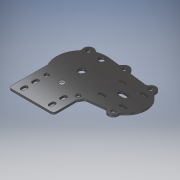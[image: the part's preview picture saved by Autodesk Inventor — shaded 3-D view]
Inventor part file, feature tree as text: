
AUTODESK INVENTOR PART (.ipt)
format: ipt  version: 2017 (Build 210142000, 142)  size: 376,320 bytes
history: native  units: mm
features: extrude x8, sketch x6, fillet x2, other x1, mirror x1
ambient origin geometry x8: Origin, YZ Plane, XZ Plane, XY Plane, X Axis, Y Axis, Z Axis, Center Point
bodies: Body1 (feature_tree)
feature tree (18):
  other  "Sólido1"
  extrude  "Extrusión1"  Depth=88.9mm
  sketch  "Boceto2"  dims[d2=203.2mm d3=22.225mm d4=22.225mm]
  extrude  "Extrusión2"  Depth=22.225mm
  fillet  "Empalme1"  Radius=22.225mm
  sketch  "Boceto3"  dims[d7=22.225mm d8=22.225mm]
  extrude  "Extrusión3"  Depth=22.225mm
  extrude  "Extrusión4"  TaperAngle=0.0deg  [1 undecoded]
  extrude  "Extrusión5"  Depth=4.445mm TaperAngle=0.0deg
  extrude  "Extrusión6"  Depth=6.35mm
  extrude  "Extrusión7"  Depth=6.35mm
  mirror  "Simetría1"
  fillet  "Empalme2"  Radius=9.525mm
  extrude  "Extrusión8"  Depth=6.35mm
  sketch  "Boceto1"  dims[d0=114.3mm d1=88.9mm]
  sketch  "Boceto4"  dims[d11=22.225mm d13=0.0mm]
  sketch  "Boceto5"  dims[d14=22.225mm d16=4.445mm d17=0.0mm]
  sketch  "Boceto7"  dims[d18=9.525mm d19=9.525mm d20=9.525mm d21=9.525mm d22=9.525mm d23=9.525mm d24=25.4mm d25=0.0mm d26=6.35mm d27=12.7mm d28=12.7mm d29=44.45mm d30=44.45mm d31=31.75mm d32=31.75mm d33=14.2875mm d34=12.7mm d35=12.7mm d36=45.0mm d37=45.0mm d38=25.4mm d39=0.0mm d40=11.1125mm d41=56.0mm d42=56.0mm d43=28.0mm d44=28.0mm d45=0.0mm d46=93.4212mm d47=47.5mm d48=47.5mm d49=23.75mm d50=23.75mm d57=5.55625mm d58=5.159375mm d59=5.55625mm d60=5.55625mm d61=5.159375mm d62=5.159375mm d63=5.55625mm d64=5.159375mm d65=0.0mm d66=5.55625mm d67=5.55625mm d68=5.159375mm d69=5.159375mm d70=0.0mm d71=5.55625mm d72=5.55625mm d73=5.159375mm d74=5.159375mm d75=0.0mm d76=25.4mm d77=0.0mm d78=11.1125mm d79=11.1125mm d80=5.159375mm d81=5.159375mm d82=101.6mm d84=171.45mm d85=95.25mm d86=25.4mm d87=0.0mm d88=25.4mm d89=0.0mm d90=8.73125mm d91=8.73125mm d92=19.05mm d93=44.45mm d94=38.1mm d95=0.0mm d96=8.73125mm d97=8.73125mm d98=19.05mm d99=19.05mm d100=12.7mm d101=0.0mm d102=25.4mm d103=0.0mm d104=6.35mm d105=25.4mm d106=0.0mm]
note: 1 required parameter value undecoded (feature->parameter linkage not recoverable at this tier; creation-order binding heuristic only, values carry confidence <= 0.55)
